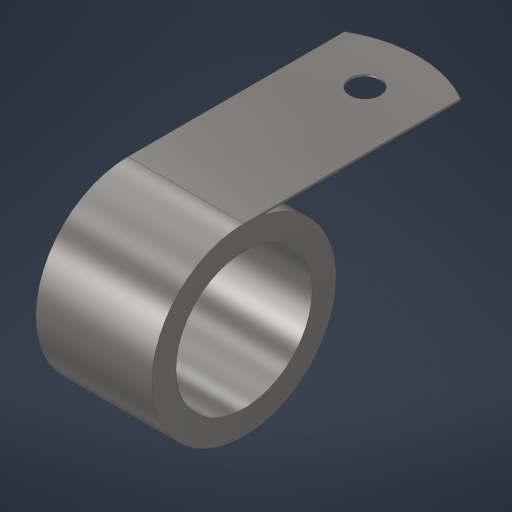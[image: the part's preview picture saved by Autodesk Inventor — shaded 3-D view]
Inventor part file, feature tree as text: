
AUTODESK INVENTOR PART (.ipt)
format: ipt  version: 2023.4 (Build 274418000, 418)  size: 202,240 bytes
history: native  units: in
note: dims shown in document units (in); Inventor stores cm internally (conversion verified against a paired STEP export)
features: plane x1, other x1
ambient origin geometry x8: Origin, YZ Plane, XZ Plane, XY Plane, X Axis, Y Axis, Z Axis, Center Point
bodies: Solid1 (feature_tree)
feature tree (2):
  plane  "Work Plane1"
  other  "OneHole"
